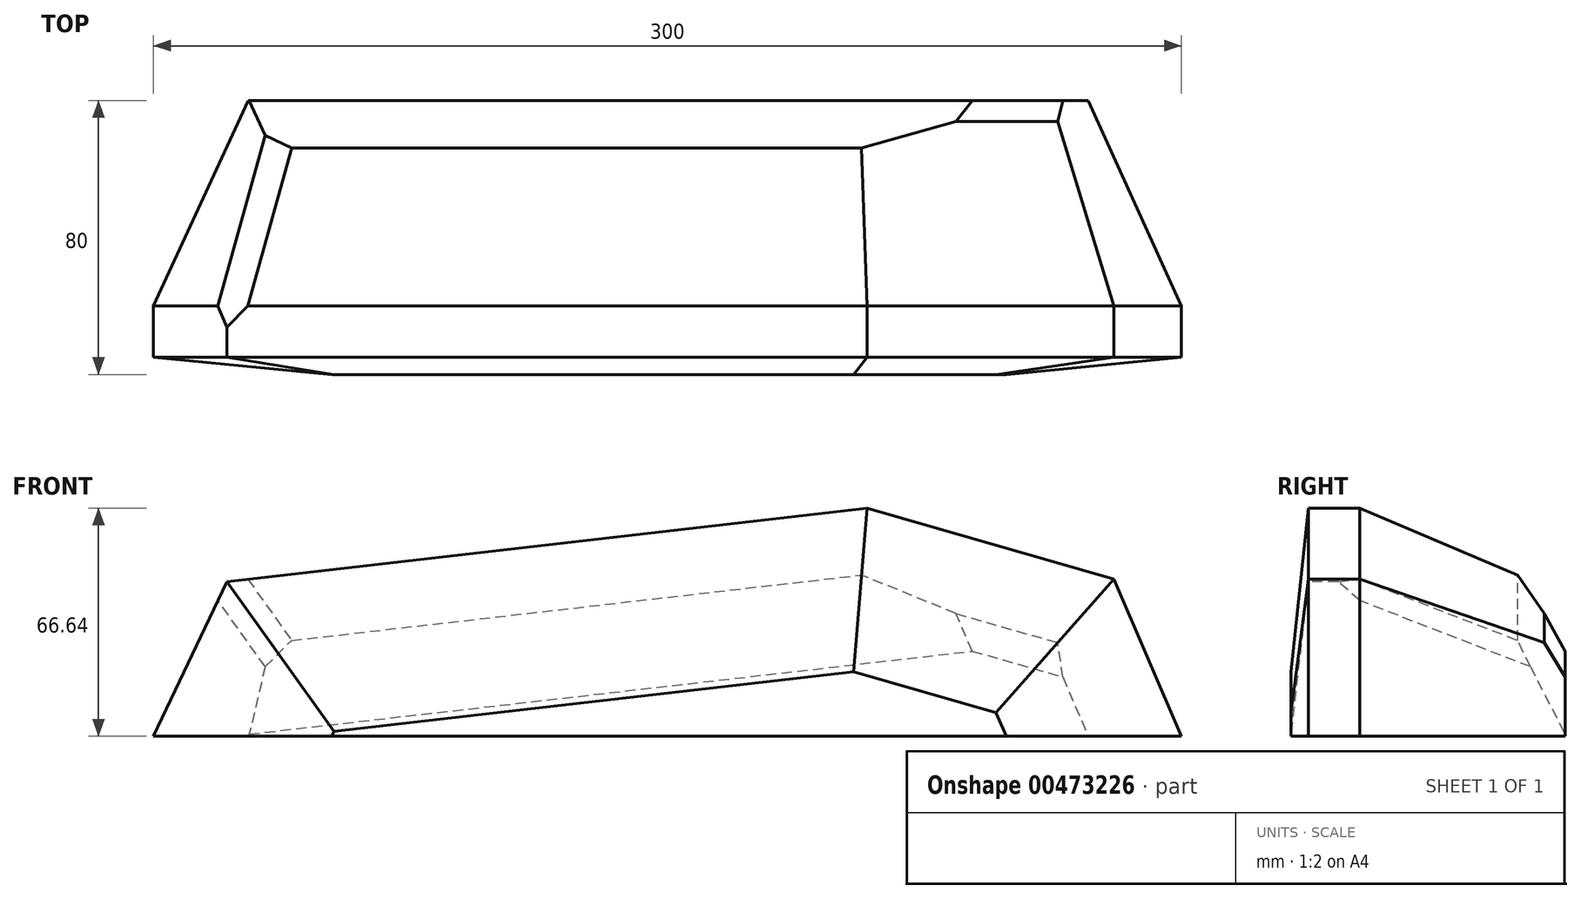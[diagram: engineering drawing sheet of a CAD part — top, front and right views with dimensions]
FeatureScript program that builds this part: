
annotation { "Feature Type Name" : "Feature", "Feature Type Description" : "" }
export const myFeature = defineFeature(function(context is Context, id is Id, definition is map)
    precondition{}
    {
        {
            var Q0;
            Q0=qCreatedBy(makeId("Front.planeOp"),FACE);
            var sketch = newSketch(context, id + "F0", { "sketchPlane" : qUnion([Q0])});
            skLineSegment(sketch, "E0", {"start": v(-145.66, -45.96) * mm, "end": v(154.34, -45.96) * mm});
            skLineSegment(sketch, "E1", {"start": v(-145.66, -45.96) * mm, "end": v(-124.22, -0.78) * mm});
            skLineSegment(sketch, "E2", {"start": v(-124.22, -0.78) * mm, "end": v(62.55, 20.68) * mm});
            skLineSegment(sketch, "E3", {"start": v(62.55, 20.68) * mm, "end": v(134.65, 0) * mm});
            skLineSegment(sketch, "E4", {"start": v(134.65, 0) * mm, "end": v(154.34, -45.96) * mm});
            skSolve(sketch);
        }
        {
            var Q0;
            Q0 = qSketchRegion(id + "F0", true);
            extrude(context, id + "F1", {"entities" : qUnion([Q0]), "oppositeDirection" : true, "depth" : 80 * mm});
        }
        {
            var Q0;
            Q0=makeQuery(id+"F1.opExtrude","CAP_EDGE",EDGE,{"disambiguationData":[OSD([sQuery(id+"F0.wireOp",EDGE,"E2")])],"isStart":false});
            var Q1;
            Q1=makeQuery(id+"F1.opExtrude","CAP_EDGE",EDGE,{"disambiguationData":[OSD([sQuery(id+"F0.wireOp",EDGE,"E3")])],"isStart":false});
            var Q2;
            Q2=makeQuery(id+"F1.opExtrude","CAP_EDGE",EDGE,{"disambiguationData":[OSD([sQuery(id+"F0.wireOp",EDGE,"E4")])],"isStart":false});
            var Q3;
            Q3=makeQuery(id+"F1.opExtrude","CAP_EDGE",EDGE,{"disambiguationData":[OSD([sQuery(id+"F0.wireOp",EDGE,"E1")])],"isStart":false});
            chamfer(context, id + "F2", {"entities" : qUnion([Q0, Q1, Q2, Q3]), "chamferType" : ChamferType.TWO_OFFSETS, "width1" : 25 * mm, "oppositeDirection" : false, "width2" : 60 * mm, "tangentPropagation" : true});
        }
        {
            var Q0;
            Q0=makeQuery(id+"F1.opExtrude","CAP_EDGE",EDGE,{"disambiguationData":[OSD([sQuery(id+"F0.wireOp",EDGE,"E2")])],"isStart":true});
            var Q1;
            Q1=makeQuery(id+"F1.opExtrude","CAP_EDGE",EDGE,{"disambiguationData":[OSD([sQuery(id+"F0.wireOp",EDGE,"E1")])],"isStart":true});
            var Q2;
            Q2=makeQuery(id+"F1.opExtrude","CAP_EDGE",EDGE,{"disambiguationData":[OSD([sQuery(id+"F0.wireOp",EDGE,"E3")])],"isStart":true});
            var Q3;
            Q3=makeQuery(id+"F1.opExtrude","CAP_EDGE",EDGE,{"disambiguationData":[OSD([sQuery(id+"F0.wireOp",EDGE,"E4")])],"isStart":true});
            chamfer(context, id + "F3", {"entities" : qUnion([Q0, Q1, Q2, Q3]), "chamferType" : ChamferType.TWO_OFFSETS, "width1" : 5 * mm, "oppositeDirection" : false, "width2" : 47 * mm, "tangentPropagation" : true});
        }
        {
            var Q0;
            {var subQ0=sQuery(id+"F0.wireOp",EDGE,"E3");Q0=makeQuery(id+"F2.opChamfer","BLEND_EDGE",EDGE,{"blendedFrom":[makeQuery(id+"F1.opExtrude","CAP_EDGE",EDGE,{"disambiguationData":[OSD([subQ0])],"isStart":false}),makeQuery(id+"F1.opExtrude","CAP_FACE",FACE,{"disambiguationData":[OSD([sQuery(id+"F0.wireOp",EDGE,"E0"),sQuery(id+"F0.wireOp",EDGE,"E1"),sQuery(id+"F0.wireOp",EDGE,"E2"),subQ0,sQuery(id+"F0.wireOp",EDGE,"E4")])],"isStart":false})],"blendedInto":[makeQuery(id+"F1.opExtrude","CAP_FACE",FACE,{"disambiguationData":[OSD([sQuery(id+"F0.wireOp",EDGE,"E0"),sQuery(id+"F0.wireOp",EDGE,"E1"),sQuery(id+"F0.wireOp",EDGE,"E2"),subQ0,sQuery(id+"F0.wireOp",EDGE,"E4")])],"isStart":false})]});}
            chamfer(context, id + "F4", {"entities" : qUnion([Q0]), "width" : 10 * mm, "tangentPropagation" : true});
        }
        {
            var Q0;
            {var subQ0=sQuery(id+"F0.wireOp",EDGE,"E2");Q0=makeQuery(id+"F2.opChamfer","BLEND_EDGE",EDGE,{"blendedFrom":[makeQuery(id+"F1.opExtrude","CAP_EDGE",EDGE,{"disambiguationData":[OSD([subQ0])],"isStart":false}),makeQuery(id+"F1.opExtrude","CAP_FACE",FACE,{"disambiguationData":[OSD([sQuery(id+"F0.wireOp",EDGE,"E0"),sQuery(id+"F0.wireOp",EDGE,"E1"),subQ0,sQuery(id+"F0.wireOp",EDGE,"E3"),sQuery(id+"F0.wireOp",EDGE,"E4")])],"isStart":false})],"blendedInto":[makeQuery(id+"F1.opExtrude","CAP_FACE",FACE,{"disambiguationData":[OSD([sQuery(id+"F0.wireOp",EDGE,"E0"),sQuery(id+"F0.wireOp",EDGE,"E1"),subQ0,sQuery(id+"F0.wireOp",EDGE,"E3"),sQuery(id+"F0.wireOp",EDGE,"E4")])],"isStart":false})]});}
            chamfer(context, id + "F5", {"entities" : qUnion([Q0]), "chamferType" : ChamferType.TWO_OFFSETS, "width1" : 20 * mm, "oppositeDirection" : false, "width2" : 15 * mm, "tangentPropagation" : true});
        }
        {
            var Q0;
            Q0=makeQuery(id+"F2.opChamfer","BLEND_EDGE",EDGE,{"blendedFrom":[makeQuery(id+"F1.opExtrude","CAP_EDGE",EDGE,{"disambiguationData":[OSD([sQuery(id+"F0.wireOp",EDGE,"E1")])],"isStart":false}),makeQuery(id+"F1.opExtrude","CAP_EDGE",EDGE,{"disambiguationData":[OSD([sQuery(id+"F0.wireOp",EDGE,"E2")])],"isStart":false})],"blendedInto":[]});
            chamfer(context, id + "F6", {"entities" : qUnion([Q0]), "width" : 12 * mm, "tangentPropagation" : true});
        }
    });
